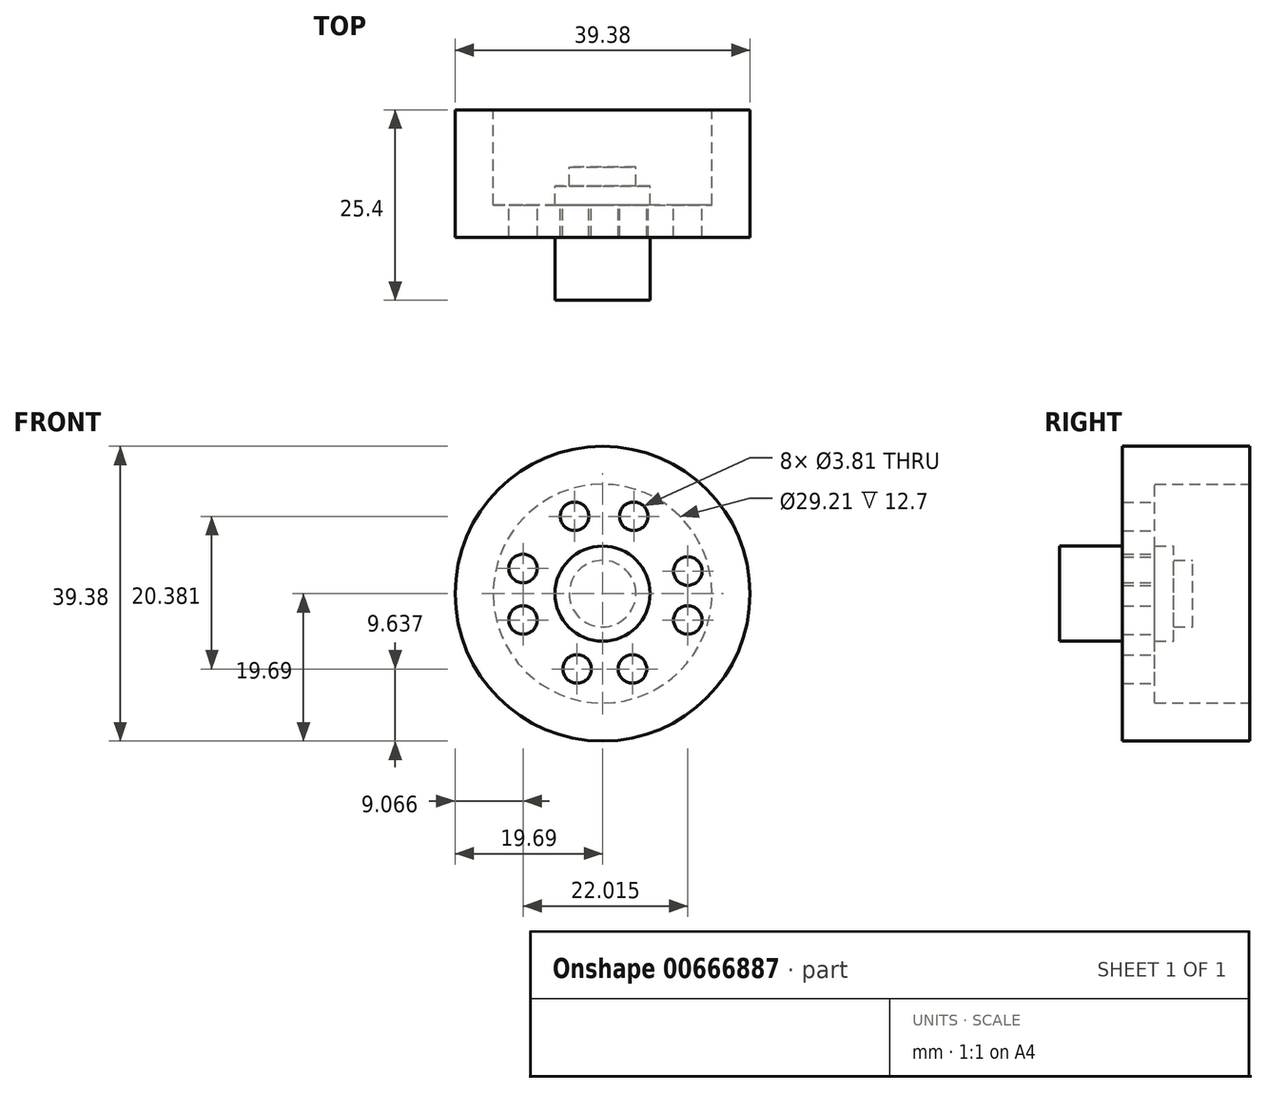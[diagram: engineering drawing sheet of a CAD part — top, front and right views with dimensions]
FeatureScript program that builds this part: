
annotation { "Feature Type Name" : "Feature", "Feature Type Description" : "" }
export const myFeature = defineFeature(function(context is Context, id is Id, definition is map)
    precondition{}
    {
        {
            var Q0;
            Q0=qCreatedBy(makeId("Front.planeOp"),FACE);
            var sketch = newSketch(context, id + "F0", { "sketchPlane" : qUnion([Q0])});
            skCircle(sketch, "E0", {"center": v(0, 0) * mm, "radius": 19.69 * mm});
            skSolve(sketch);
        }
        {
            var Q0;
            Q0 = qSketchRegion(id + "F0", true);
            extrude(context, id + "F1", {"entities" : qUnion([Q0]), "depth" : 17.02 * mm, "offsetDistance" : 25.4 * mm});
        }
        {
            var Q0;
            Q0=qCreatedBy(makeId("Front.planeOp"),FACE);
            var sketch = newSketch(context, id + "F2", { "sketchPlane" : qUnion([Q0])});
            skCircle(sketch, "E1", {"center": v(0, 0) * mm, "radius": 14.6 * mm});
            skSolve(sketch);
        }
        {
            var Q0;
            Q0 = qSketchRegion(id + "F2", true);
            extrude(context, id + "F3", {"entities" : qUnion([Q0]), "operationType" : NewBodyOperationType.REMOVE, "depth" : 12.7 * mm, "offsetDistance" : 25.4 * mm});
        }
        {
            var Q0;
            Q0=qCreatedBy(makeId("Front.planeOp"),FACE);
            var sketch = newSketch(context, id + "F4", { "sketchPlane" : qUnion([Q0])});
            skCircle(sketch, "E2", {"center": v(-3.74, 10.33) * mm, "radius": 1.9 * mm});
            skCircle(sketch, "E3", {"center": v(-10.62, 3.36) * mm, "radius": 1.9 * mm});
            skCircle(sketch, "E4", {"center": v(-10.62, -3.52) * mm, "radius": 1.9 * mm});
            skCircle(sketch, "E5", {"center": v(-3.4, -10.05) * mm, "radius": 1.9 * mm});
            skCircle(sketch, "E6", {"center": v(4, -10.05) * mm, "radius": 1.9 * mm});
            skCircle(sketch, "E7", {"center": v(11.4, -3.52) * mm, "radius": 1.9 * mm});
            skCircle(sketch, "E8", {"center": v(4.17, 10.33) * mm, "radius": 1.9 * mm});
            skCircle(sketch, "E9", {"center": v(11.4, 3.02) * mm, "radius": 1.9 * mm});
            skSolve(sketch);
        }
        {
            var Q0;
            Q0 = qSketchRegion(id + "F4", true);
            extrude(context, id + "F5", {"entities" : qUnion([Q0]), "operationType" : NewBodyOperationType.REMOVE, "depth" : 21.34 * mm, "offsetDistance" : 25.4 * mm});
        }
        {
            var Q0;
            Q0=qCreatedBy(makeId("Front.planeOp"),FACE);
            var sketch = newSketch(context, id + "F6", { "sketchPlane" : qUnion([Q0])});
            skCircle(sketch, "E10", {"center": v(0, 0) * mm, "radius": 6.35 * mm});
            skSolve(sketch);
        }
        {
            var Q0;
            Q0 = qSketchRegion(id + "F6", true);
            extrude(context, id + "F7", {"entities" : qUnion([Q0]), "operationType" : NewBodyOperationType.ADD, "depth" : 25.4 * mm, "offsetDistance" : 25.4 * mm});
        }
        {
            var Q0;
            Q0=makeQuery(id+"F7.opExtrude","CAP_FACE",FACE,{"disambiguationData":[OSD([sQuery(id+"F6.wireOp",EDGE,"E10")])],"isStart":true});
            extrude(context, id + "F8", {"entities" : qUnion([Q0]), "operationType" : NewBodyOperationType.REMOVE, "oppositeDirection" : true, "depth" : 10.16 * mm, "offsetDistance" : 25.4 * mm});
        }
        {
            var Q0;
            Q0=qCreatedBy(makeId("Front.planeOp"),FACE);
            var sketch = newSketch(context, id + "F9", { "sketchPlane" : qUnion([Q0])});
            skCircle(sketch, "E11", {"center": v(0, 0) * mm, "radius": 4.45 * mm});
            skSolve(sketch);
        }
        {
            var Q0;
            Q0 = qSketchRegion(id + "F9", true);
            extrude(context, id + "F10", {"entities" : qUnion([Q0]), "operationType" : NewBodyOperationType.ADD, "depth" : 25.4 * mm, "offsetDistance" : 25.4 * mm});
        }
        {
            var Q0;
            Q0=makeQuery(id+"F10.opExtrude","CAP_FACE",FACE,{"disambiguationData":[OSD([sQuery(id+"F9.wireOp",EDGE,"E11")])],"isStart":true});
            extrude(context, id + "F11", {"entities" : qUnion([Q0]), "operationType" : NewBodyOperationType.REMOVE, "oppositeDirection" : true, "depth" : 7.62 * mm, "offsetDistance" : 25.4 * mm});
        }
    });
